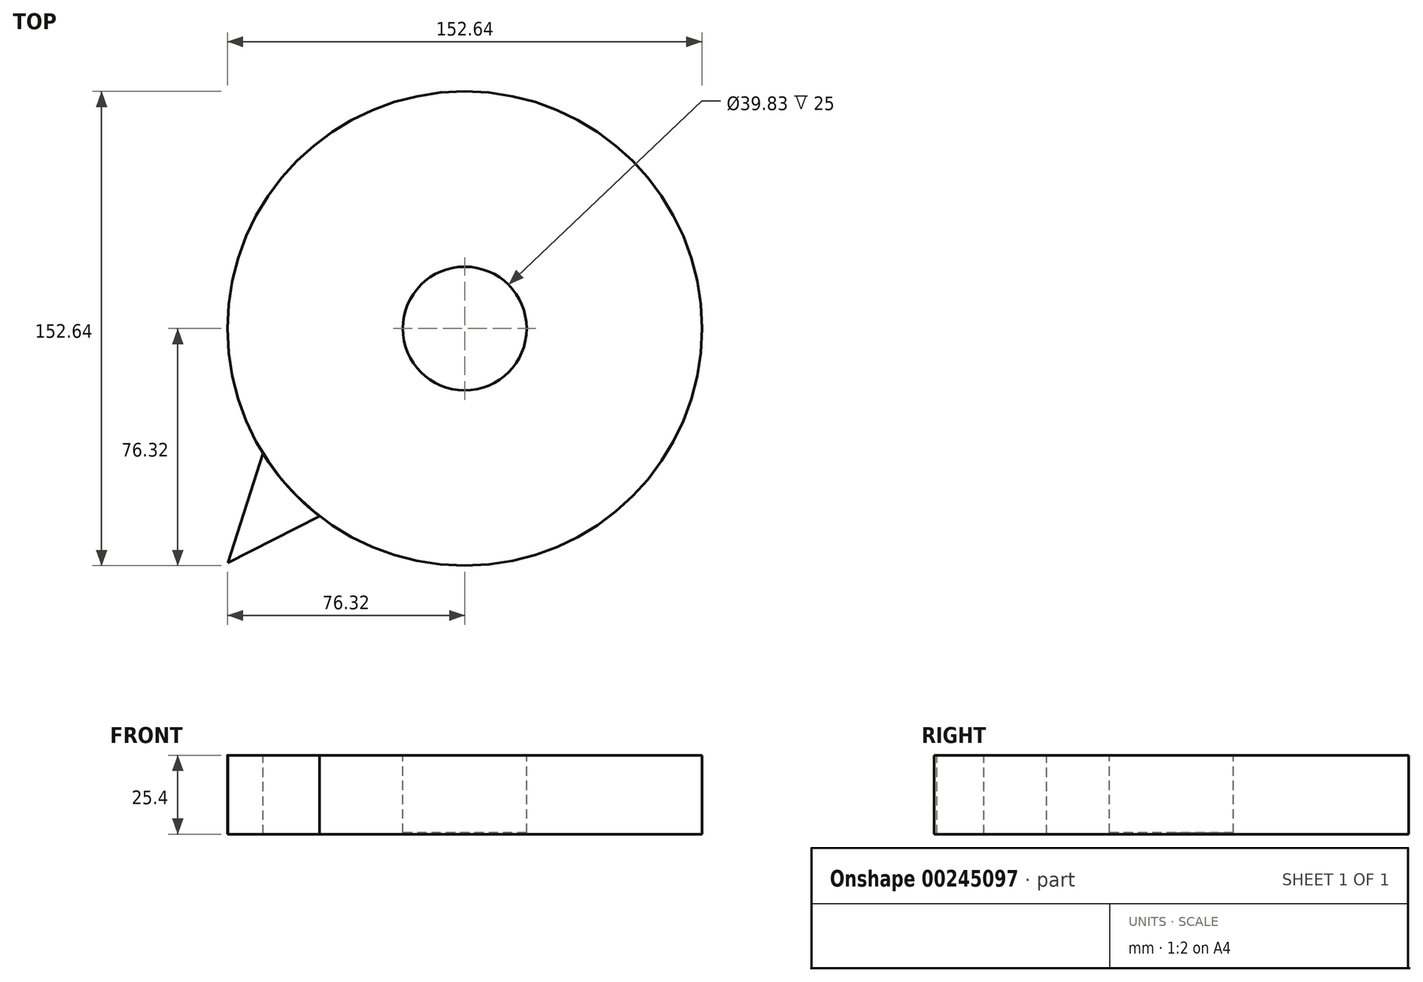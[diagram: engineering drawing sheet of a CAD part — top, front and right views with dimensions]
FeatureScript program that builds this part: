
annotation { "Feature Type Name" : "Feature", "Feature Type Description" : "" }
export const myFeature = defineFeature(function(context is Context, id is Id, definition is map)
    precondition{}
    {
        {
            var Q0;
            Q0=qCreatedBy(makeId("Top.planeOp"),FACE);
            var sketch = newSketch(context, id + "F0", { "sketchPlane" : qUnion([Q0])});
            skCircle(sketch, "E0", {"center": v(0, 0) * mm, "radius": 76.32 * mm});
            skSolve(sketch);
        }
        {
            var Q0;
            Q0=makeQuery(id+"F0.imprint","IMPRINT",FACE,{"disambiguationData":[TD([[makeQuery(id+"F0.imprint","IMPRINT",EDGE,{"derivedFrom":sQuery(id+"F0.wireOp",EDGE,"E0")}),1.0]])]});
            extrude(context, id + "F1", {"entities" : qUnion([Q0]), "depth" : 25.4 * mm});
        }
        {
            var Q0;
            Q0=makeQuery(id+"F1.opExtrude","CAP_FACE",FACE,{"disambiguationData":[OSD([sQuery(id+"F0.wireOp",EDGE,"E0")])],"isStart":false});
            var sketch = newSketch(context, id + "F2", { "sketchPlane" : qUnion([Q0])});
            skLineSegment(sketch, "E1", {"start": v(-64.9, -40.14) * mm, "end": v(-76.2, -75.4) * mm});
            skLineSegment(sketch, "E2", {"start": v(-76.2, -75.4) * mm, "end": v(-46.72, -60.34) * mm});
            skSolve(sketch);
        }
        {
            var Q0;
            {var subQ0=sQuery(id+"F2.wireOp",EDGE,"E1");Q0=makeQuery(id+"F2.imprint","IMPRINT",FACE,{"disambiguationData":[TD([[makeQuery(id+"F2.imprint","IMPRINT",EDGE,{"derivedFrom":subQ0}),1.0]])]});}
            extrude(context, id + "F3", {"entities" : qUnion([Q0]), "oppositeDirection" : true, "depth" : 25.4 * mm});
        }
        {
            var Q0;
            Q0=makeQuery(id+"F1.opExtrude","CAP_FACE",FACE,{"disambiguationData":[OSD([sQuery(id+"F0.wireOp",EDGE,"E0")])],"isStart":false});
            var sketch = newSketch(context, id + "F4", { "sketchPlane" : qUnion([Q0])});
            skCircle(sketch, "E3", {"center": v(0, 0) * mm, "radius": 68 * mm});
            skCircle(sketch, "E4", {"center": v(0, 0) * mm, "radius": 56.08 * mm});
            skCircle(sketch, "E5", {"center": v(0, 0) * mm, "radius": 44.46 * mm});
            skSolve(sketch);
        }
        {
            var Q0;
            Q0=makeQuery(id+"F4.imprint","IMPRINT",FACE,{"disambiguationData":[TD([[makeQuery(id+"F4.imprint","IMPRINT",EDGE,{"derivedFrom":sQuery(id+"F4.wireOp",EDGE,"E3")}),1.0]])]});
            extrude(context, id + "F5", {"entities" : qUnion([Q0]), "operationType" : NewBodyOperationType.ADD, "oppositeDirection" : true, "depth" : 25.4 * mm});
        }
        {
            var Q0;
            Q0=makeQuery(id+"F1.opExtrude","CAP_FACE",FACE,{"disambiguationData":[OSD([sQuery(id+"F0.wireOp",EDGE,"E0")])],"isStart":false});
            var sketch = newSketch(context, id + "F6", { "sketchPlane" : qUnion([Q0])});
            skCircle(sketch, "E6", {"center": v(0, 0) * mm, "radius": 19.91 * mm});
            skSolve(sketch);
        }
        {
            var Q0;
            Q0=makeQuery(id+"F6.imprint","IMPRINT",FACE,{"disambiguationData":[TD([[makeQuery(id+"F6.imprint","IMPRINT",EDGE,{"derivedFrom":sQuery(id+"F6.wireOp",EDGE,"E6")}),1.0]])]});
            extrude(context, id + "F7", {"entities" : qUnion([Q0]), "operationType" : NewBodyOperationType.REMOVE, "oppositeDirection" : true, "depth" : 25 * mm});
        }
    });
